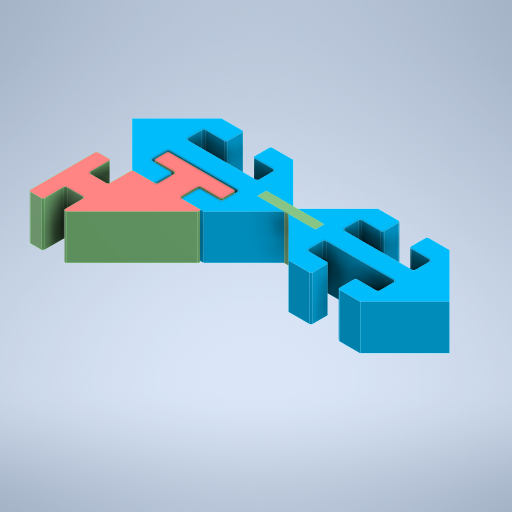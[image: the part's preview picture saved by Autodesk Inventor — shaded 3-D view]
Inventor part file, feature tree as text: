
AUTODESK INVENTOR PART (.ipt)
format: ipt  version: 2023 (Build 270158000, 158)  size: 449,536 bytes
history: native  units: in
note: dims shown in document units (in); Inventor stores cm internally (conversion verified against a paired STEP export)
features: other x3, extrude x3, fillet x3, sketch x1
ambient origin geometry x8: Origin, YZ Plane, XZ Plane, XY Plane, X Axis, Y Axis, Z Axis, Center Point
bodies: Body1 (feature_tree), Body2 (feature_tree), Body3 (feature_tree)
feature tree (10):
  other  "PLA"
  sketch  "Sketch1"  dims[d0=0.4921in d1=0.3937in d2=0.1969in d3=0.1969in d4=0.1181in d5=0.0197in d6=0.0787in d7=0.0787in d8=0.1575in d9=0.0591in d10=0.0984in d11=0.0098in d12=45.0deg d13=0.1969in d14=0.0in d15=0.1969in d16=0.0in d17=0.0079in d18=0.0984in d19=0.1969in d20=0.0in d21=0.0079in d25=0.0079in d26=0.0079in]
  extrude  "Extrusion1"  Depth=0.3937in
  extrude  "Extrusion2"  Depth=0.1969in
  fillet  "Fillet1"  Radius=0.1969in
  extrude  "Extrusion3"  Depth=0.1181in
  fillet  "Fillet2"  Radius=0.0197in
  fillet  "Fillet3"  Radius=0.0787in
  other  "TPU"
  other  "PLA2"
